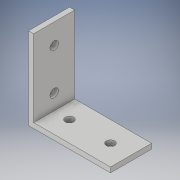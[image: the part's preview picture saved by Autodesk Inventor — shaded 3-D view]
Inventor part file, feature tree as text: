
AUTODESK INVENTOR PART (.ipt)
format: ipt  version: 2018 (Build 220112000, 112)  size: 122,880 bytes
history: native  units: in
note: dims shown in document units (in); Inventor stores cm internally (conversion verified against a paired STEP export)
features: extrude x3, sketch x3
ambient origin geometry x8: Origin, YZ Plane, XZ Plane, XY Plane, X Axis, Y Axis, Z Axis, Center Point
bodies: Solid1 (feature_tree)
feature tree (6):
  extrude  "Extrusion1"  Depth=2.0in
  extrude  "Extrusion2"  Depth=0.125in
  extrude  "Extrusion3"  Depth=1.0in TaperAngle=0.0deg
  sketch  "Sketch1"  dims[d0=0.125in d1=2.0in]
  sketch  "Sketch2"  dims[d2=2.0in d3=0.125in]
  sketch  "Sketch3"  dims[d4=1.0in d5=0.0in d10=1.0in d11=0.0in d12=0.375in d13=0.2031in d14=1.0in d15=0.2031in d16=1.0in d17=0.0in d18=0.375in d19=0.2031in d22=1.0in d23=0.2031in]
